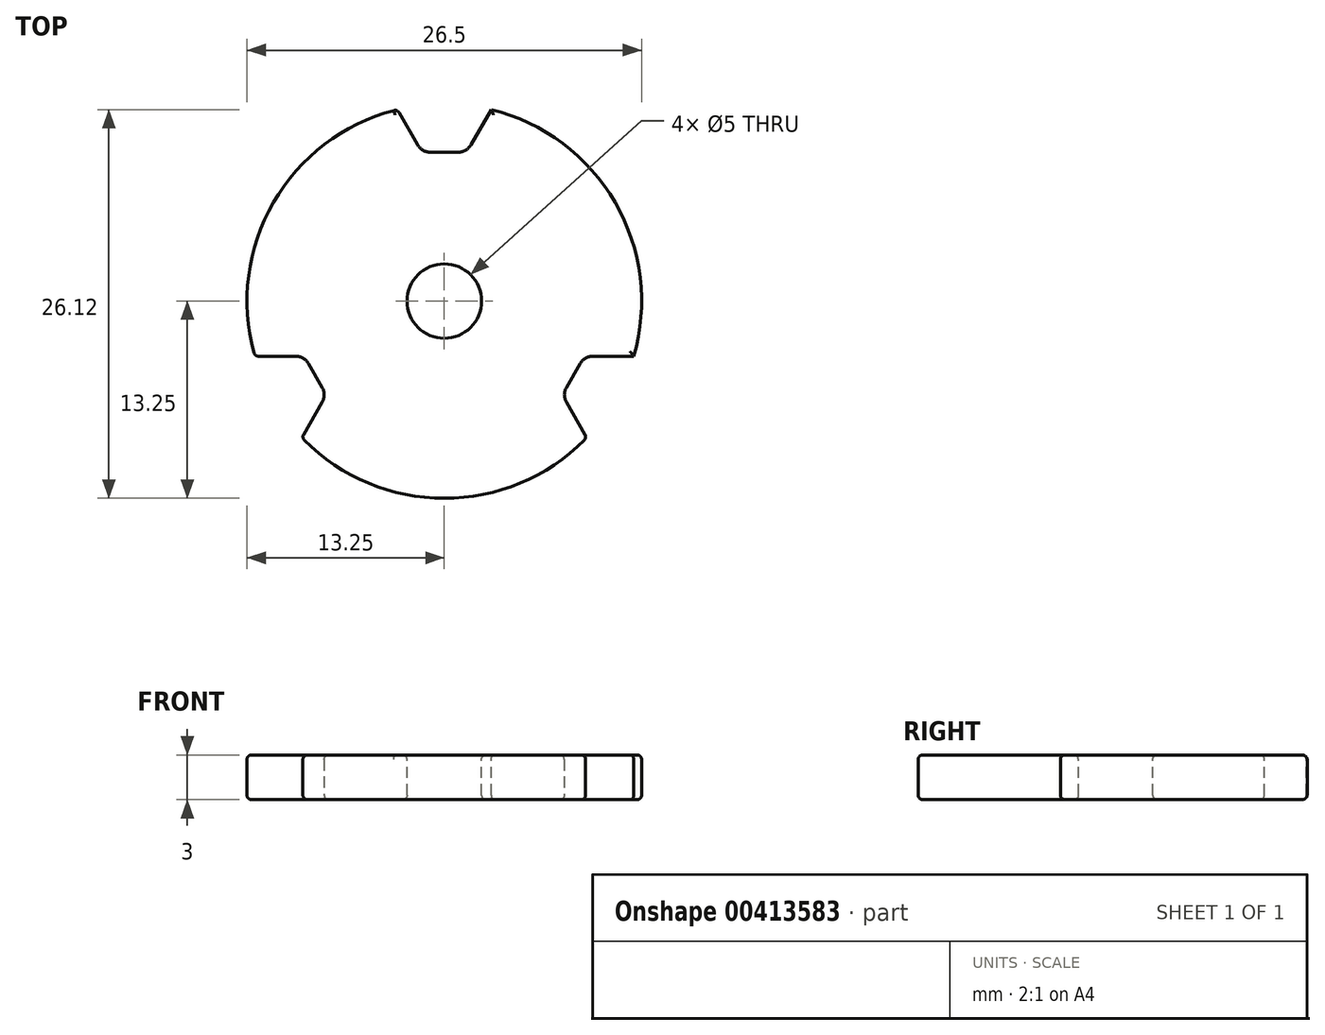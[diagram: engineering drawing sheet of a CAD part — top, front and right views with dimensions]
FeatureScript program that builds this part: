
annotation { "Feature Type Name" : "Feature", "Feature Type Description" : "" }
export const myFeature = defineFeature(function(context is Context, id is Id, definition is map)
    precondition{}
    {
        {
            var Q0;
            Q0=qCreatedBy(makeId("Front.planeOp"),FACE);
            var sketch = newSketch(context, id + "F0", { "sketchPlane" : qUnion([Q0])});
            skLineSegment(sketch, "E0", {"start": v(0, 0) * mm, "end": v(0, -3) * mm, "construction": true});
            skLineSegment(sketch, "E1", {"start": v(2.5, 0) * mm, "end": v(2.5, -3) * mm});
            skLineSegment(sketch, "E2", {"start": v(2.5, -3) * mm, "end": v(13.25, -3) * mm});
            skLineSegment(sketch, "E3", {"start": v(13.25, -3) * mm, "end": v(13.25, -3) * mm});
            skLineSegment(sketch, "E4", {"start": v(13.25, -3) * mm, "end": v(13.25, 0) * mm});
            skLineSegment(sketch, "E5", {"start": v(13.25, 0) * mm, "end": v(13.25, 0) * mm});
            skLineSegment(sketch, "E6", {"start": v(13.25, 0) * mm, "end": v(2.5, 0) * mm});
            skSolve(sketch);
        }
        {
            var Q0;
            Q0=makeQuery(id+"F0.imprint","IMPRINT",FACE,{"disambiguationData":[TD([[makeQuery(id+"F0.imprint","IMPRINT",EDGE,{"derivedFrom":sQuery(id+"F0.wireOp",EDGE,"E1")}),1.0]])]});
            var Q1;
            Q1=sQuery(id+"F0.wireOp",EDGE,"E0");
            revolve(context, id + "F1", {"entities" : qUnion([Q0]), "axis" : qUnion([Q1]), "revolveType" : RevolveType.FULL});
        }
        {
            var Q0;
            Q0=makeQuery(id+"F1.opRevolve","SWEPT_FACE",FACE,{"disambiguationData":[OSD([sQuery(id+"F0.wireOp",EDGE,"E6")])]});
            var sketch = newSketch(context, id + "F2", { "sketchPlane" : qUnion([Q0])});
            skArc(sketch, "E7.0", {"start": v(3.16, 12.87) * mm, "mid": v(0, 13.25) * mm, "end": v(-3.16, 12.87) * mm});
            skLineSegment(sketch, "E8", {"start": v(-3.16, 12.87) * mm, "end": v(-1.5, 10) * mm});
            skLineSegment(sketch, "E9", {"start": v(-1.5, 10) * mm, "end": v(1.5, 10) * mm});
            skLineSegment(sketch, "E10", {"start": v(1.5, 10) * mm, "end": v(3.16, 12.87) * mm});
            skLineSegment(sketch, "E11", {"start": v(0, 0) * mm, "end": v(0, 10) * mm, "construction": true});
            skLineSegment(sketch, "E12.1.0", {"start": v(-9.57, -9.17) * mm, "end": v(-7.91, -6.3) * mm});
            skArc(sketch, "E12.1.1", {"start": v(-12.72, -3.7) * mm, "mid": v(-11.47, -6.62) * mm, "end": v(-9.57, -9.17) * mm});
            skLineSegment(sketch, "E12.1.2", {"start": v(-9.41, -3.7) * mm, "end": v(-12.72, -3.7) * mm});
            skLineSegment(sketch, "E12.1.3", {"start": v(-7.91, -6.3) * mm, "end": v(-9.41, -3.7) * mm});
            skLineSegment(sketch, "E12.2.0", {"start": v(12.72, -3.7) * mm, "end": v(9.41, -3.7) * mm});
            skArc(sketch, "E12.2.1", {"start": v(9.57, -9.17) * mm, "mid": v(11.47, -6.63) * mm, "end": v(12.72, -3.7) * mm});
            skLineSegment(sketch, "E12.2.2", {"start": v(7.91, -6.3) * mm, "end": v(9.57, -9.17) * mm});
            skLineSegment(sketch, "E12.2.3", {"start": v(9.41, -3.7) * mm, "end": v(7.91, -6.3) * mm});
            skSolve(sketch);
        }
        {
            var Q0;
            Q0 = qSketchRegion(id + "F2", true);
            extrude(context, id + "F3", {"entities" : qUnion([Q0]), "operationType" : NewBodyOperationType.REMOVE, "oppositeDirection" : true, "depth" : 25 * mm});
        }
        {
            var Q0;
            Q0=makeQuery(id+"F3.boolean.opBoolean","COPY",EDGE,{"derivedFrom":makeQuery(id+"F3.opExtrude","SWEPT_EDGE",EDGE,{"disambiguationData":[OSD([sQuery(id+"F2.wireOp",EDGE,"E12.1.2"),sQuery(id+"F2.wireOp",EDGE,"E12.1.3")])]})});
            var Q1;
            Q1=makeQuery(id+"F3.boolean.opBoolean","COPY",EDGE,{"derivedFrom":makeQuery(id+"F3.opExtrude","SWEPT_EDGE",EDGE,{"disambiguationData":[OSD([sQuery(id+"F2.wireOp",EDGE,"E12.1.0"),sQuery(id+"F2.wireOp",EDGE,"E12.1.3")])]})});
            var Q2;
            Q2=makeQuery(id+"F3.boolean.opBoolean","COPY",EDGE,{"derivedFrom":makeQuery(id+"F3.opExtrude","SWEPT_EDGE",EDGE,{"disambiguationData":[OSD([sQuery(id+"F2.wireOp",EDGE,"E12.2.2"),sQuery(id+"F2.wireOp",EDGE,"E12.2.3")])]})});
            var Q3;
            Q3=makeQuery(id+"F3.boolean.opBoolean","COPY",EDGE,{"derivedFrom":makeQuery(id+"F3.opExtrude","SWEPT_EDGE",EDGE,{"disambiguationData":[OSD([sQuery(id+"F2.wireOp",EDGE,"E12.2.0"),sQuery(id+"F2.wireOp",EDGE,"E12.2.3")])]})});
            var Q4;
            Q4=makeQuery(id+"F3.boolean.opBoolean","COPY",EDGE,{"derivedFrom":makeQuery(id+"F3.opExtrude","SWEPT_EDGE",EDGE,{"disambiguationData":[OSD([sQuery(id+"F2.wireOp",EDGE,"E9"),sQuery(id+"F2.wireOp",EDGE,"E10")])]})});
            var Q5;
            Q5=makeQuery(id+"F3.boolean.opBoolean","COPY",EDGE,{"derivedFrom":makeQuery(id+"F3.opExtrude","SWEPT_EDGE",EDGE,{"disambiguationData":[OSD([sQuery(id+"F2.wireOp",EDGE,"E8"),sQuery(id+"F2.wireOp",EDGE,"E9")])]})});
            fillet(context, id + "F4", {"entities" : qUnion([Q0, Q1, Q2, Q3, Q4, Q5]), "radius" : 1 * mm, "tangentPropagation" : true, "allowEdgeOverflow" : false});
        }
        {
            var Q0;
            Q0=makeQuery(id+"F1.opRevolve","SWEPT_FACE",FACE,{"disambiguationData":[OSD([sQuery(id+"F0.wireOp",EDGE,"E6")])]});
            var Q1;
            Q1=makeQuery(id+"F3.boolean.opBoolean","COPY",EDGE,{"derivedFrom":makeQuery(id+"F3.opExtrude","SWEPT_EDGE",EDGE,{"disambiguationData":[OSD([sQuery(id+"F2.wireOp",EDGE,"E12.2.0"),sQuery(id+"F2.wireOp",EDGE,"E12.2.1")])]})});
            var Q2;
            Q2=makeQuery(id+"F3.boolean.opBoolean","INTERSECT",EDGE,{"derivedFrom":[makeQuery(id+"F1.opRevolve","SWEPT_FACE",FACE,{"disambiguationData":[OSD([sQuery(id+"F0.wireOp",EDGE,"E5")])]}),makeQuery(id+"F3.opExtrude","SWEPT_FACE",FACE,{"disambiguationData":[OSD([sQuery(id+"F2.wireOp",EDGE,"E12.2.0")])]})]});
            var Q3;
            Q3=makeQuery(id+"F3.boolean.opBoolean","INTERSECT",EDGE,{"derivedFrom":[makeQuery(id+"F1.opRevolve","SWEPT_FACE",FACE,{"disambiguationData":[OSD([sQuery(id+"F0.wireOp",EDGE,"E5")])]}),makeQuery(id+"F3.opExtrude","SWEPT_FACE",FACE,{"disambiguationData":[OSD([sQuery(id+"F2.wireOp",EDGE,"E12.2.2")])]})]});
            var Q4;
            Q4=makeQuery(id+"F3.boolean.opBoolean","COPY",EDGE,{"derivedFrom":makeQuery(id+"F3.opExtrude","SWEPT_EDGE",EDGE,{"disambiguationData":[OSD([sQuery(id+"F2.wireOp",EDGE,"E12.2.1"),sQuery(id+"F2.wireOp",EDGE,"E12.2.2")])]})});
            var Q5;
            Q5=makeQuery(id+"F3.boolean.opBoolean","INTERSECT",EDGE,{"derivedFrom":[makeQuery(id+"F1.opRevolve","SWEPT_FACE",FACE,{"disambiguationData":[OSD([sQuery(id+"F0.wireOp",EDGE,"E5")])]}),makeQuery(id+"F3.opExtrude","SWEPT_FACE",FACE,{"disambiguationData":[OSD([sQuery(id+"F2.wireOp",EDGE,"E12.1.0")])]})]});
            var Q6;
            Q6=makeQuery(id+"F3.boolean.opBoolean","COPY",EDGE,{"derivedFrom":makeQuery(id+"F3.opExtrude","SWEPT_EDGE",EDGE,{"disambiguationData":[OSD([sQuery(id+"F2.wireOp",EDGE,"E12.1.0"),sQuery(id+"F2.wireOp",EDGE,"E12.1.1")])]})});
            var Q7;
            Q7=makeQuery(id+"F3.boolean.opBoolean","INTERSECT",EDGE,{"derivedFrom":[makeQuery(id+"F1.opRevolve","SWEPT_FACE",FACE,{"disambiguationData":[OSD([sQuery(id+"F0.wireOp",EDGE,"E3")])]}),makeQuery(id+"F3.opExtrude","SWEPT_FACE",FACE,{"disambiguationData":[OSD([sQuery(id+"F2.wireOp",EDGE,"E12.1.0")])]})]});
            var Q8;
            Q8=makeQuery(id+"F3.boolean.opBoolean","INTERSECT",EDGE,{"derivedFrom":[makeQuery(id+"F1.opRevolve","SWEPT_FACE",FACE,{"disambiguationData":[OSD([sQuery(id+"F0.wireOp",EDGE,"E5")])]}),makeQuery(id+"F3.opExtrude","SWEPT_FACE",FACE,{"disambiguationData":[OSD([sQuery(id+"F2.wireOp",EDGE,"E12.1.2")])]})]});
            var Q9;
            Q9=makeQuery(id+"F3.boolean.opBoolean","COPY",EDGE,{"derivedFrom":makeQuery(id+"F3.opExtrude","SWEPT_EDGE",EDGE,{"disambiguationData":[OSD([sQuery(id+"F2.wireOp",EDGE,"E12.1.1"),sQuery(id+"F2.wireOp",EDGE,"E12.1.2")])]})});
            var Q10;
            Q10=makeQuery(id+"F3.boolean.opBoolean","INTERSECT",EDGE,{"derivedFrom":[makeQuery(id+"F1.opRevolve","SWEPT_FACE",FACE,{"disambiguationData":[OSD([sQuery(id+"F0.wireOp",EDGE,"E3")])]}),makeQuery(id+"F3.opExtrude","SWEPT_FACE",FACE,{"disambiguationData":[OSD([sQuery(id+"F2.wireOp",EDGE,"E12.1.2")])]})]});
            var Q11;
            Q11=makeQuery(id+"F3.boolean.opBoolean","INTERSECT",EDGE,{"derivedFrom":[makeQuery(id+"F1.opRevolve","SWEPT_FACE",FACE,{"disambiguationData":[OSD([sQuery(id+"F0.wireOp",EDGE,"E3")])]}),makeQuery(id+"F3.opExtrude","SWEPT_FACE",FACE,{"disambiguationData":[OSD([sQuery(id+"F2.wireOp",EDGE,"E12.2.2")])]})]});
            var Q12;
            Q12=makeQuery(id+"F3.boolean.opBoolean","INTERSECT",EDGE,{"derivedFrom":[makeQuery(id+"F1.opRevolve","SWEPT_FACE",FACE,{"disambiguationData":[OSD([sQuery(id+"F0.wireOp",EDGE,"E3")])]}),makeQuery(id+"F3.opExtrude","SWEPT_FACE",FACE,{"disambiguationData":[OSD([sQuery(id+"F2.wireOp",EDGE,"E12.2.0")])]})]});
            var Q13;
            Q13=makeQuery(id+"F1.opRevolve","SWEPT_FACE",FACE,{"disambiguationData":[OSD([sQuery(id+"F0.wireOp",EDGE,"E2")])]});
            var Q14;
            Q14=makeQuery(id+"F3.boolean.opBoolean","INTERSECT",EDGE,{"derivedFrom":[makeQuery(id+"F1.opRevolve","SWEPT_FACE",FACE,{"disambiguationData":[OSD([sQuery(id+"F0.wireOp",EDGE,"E5")])]}),makeQuery(id+"F3.opExtrude","SWEPT_FACE",FACE,{"disambiguationData":[OSD([sQuery(id+"F2.wireOp",EDGE,"E8")])]})]});
            var Q15;
            Q15=makeQuery(id+"F3.boolean.opBoolean","COPY",EDGE,{"derivedFrom":makeQuery(id+"F3.opExtrude","SWEPT_EDGE",EDGE,{"disambiguationData":[OSD([sQuery(id+"F2.wireOp",EDGE,"E7.0"),sQuery(id+"F2.wireOp",EDGE,"E8")])]})});
            var Q16;
            Q16=makeQuery(id+"F3.boolean.opBoolean","INTERSECT",EDGE,{"derivedFrom":[makeQuery(id+"F1.opRevolve","SWEPT_FACE",FACE,{"disambiguationData":[OSD([sQuery(id+"F0.wireOp",EDGE,"E3")])]}),makeQuery(id+"F3.opExtrude","SWEPT_FACE",FACE,{"disambiguationData":[OSD([sQuery(id+"F2.wireOp",EDGE,"E8")])]})]});
            var Q17;
            Q17=makeQuery(id+"F3.boolean.opBoolean","INTERSECT",EDGE,{"derivedFrom":[makeQuery(id+"F1.opRevolve","SWEPT_FACE",FACE,{"disambiguationData":[OSD([sQuery(id+"F0.wireOp",EDGE,"E3")])]}),makeQuery(id+"F3.opExtrude","SWEPT_FACE",FACE,{"disambiguationData":[OSD([sQuery(id+"F2.wireOp",EDGE,"E10")])]})]});
            var Q18;
            Q18=makeQuery(id+"F3.boolean.opBoolean","INTERSECT",EDGE,{"derivedFrom":[makeQuery(id+"F1.opRevolve","SWEPT_FACE",FACE,{"disambiguationData":[OSD([sQuery(id+"F0.wireOp",EDGE,"E5")])]}),makeQuery(id+"F3.opExtrude","SWEPT_FACE",FACE,{"disambiguationData":[OSD([sQuery(id+"F2.wireOp",EDGE,"E10")])]})]});
            var Q19;
            Q19=makeQuery(id+"F3.boolean.opBoolean","COPY",EDGE,{"derivedFrom":makeQuery(id+"F3.opExtrude","SWEPT_EDGE",EDGE,{"disambiguationData":[OSD([sQuery(id+"F2.wireOp",EDGE,"E7.0"),sQuery(id+"F2.wireOp",EDGE,"E10")])]})});
            fillet(context, id + "F5", {"entities" : qUnion([Q0, Q1, Q2, Q3, Q4, Q5, Q6, Q7, Q8, Q9, Q10, Q11, Q12, Q13, Q14, Q15, Q16, Q17, Q18, Q19]), "radius" : .3 * mm, "tangentPropagation" : true, "allowEdgeOverflow" : false});
        }
    });
